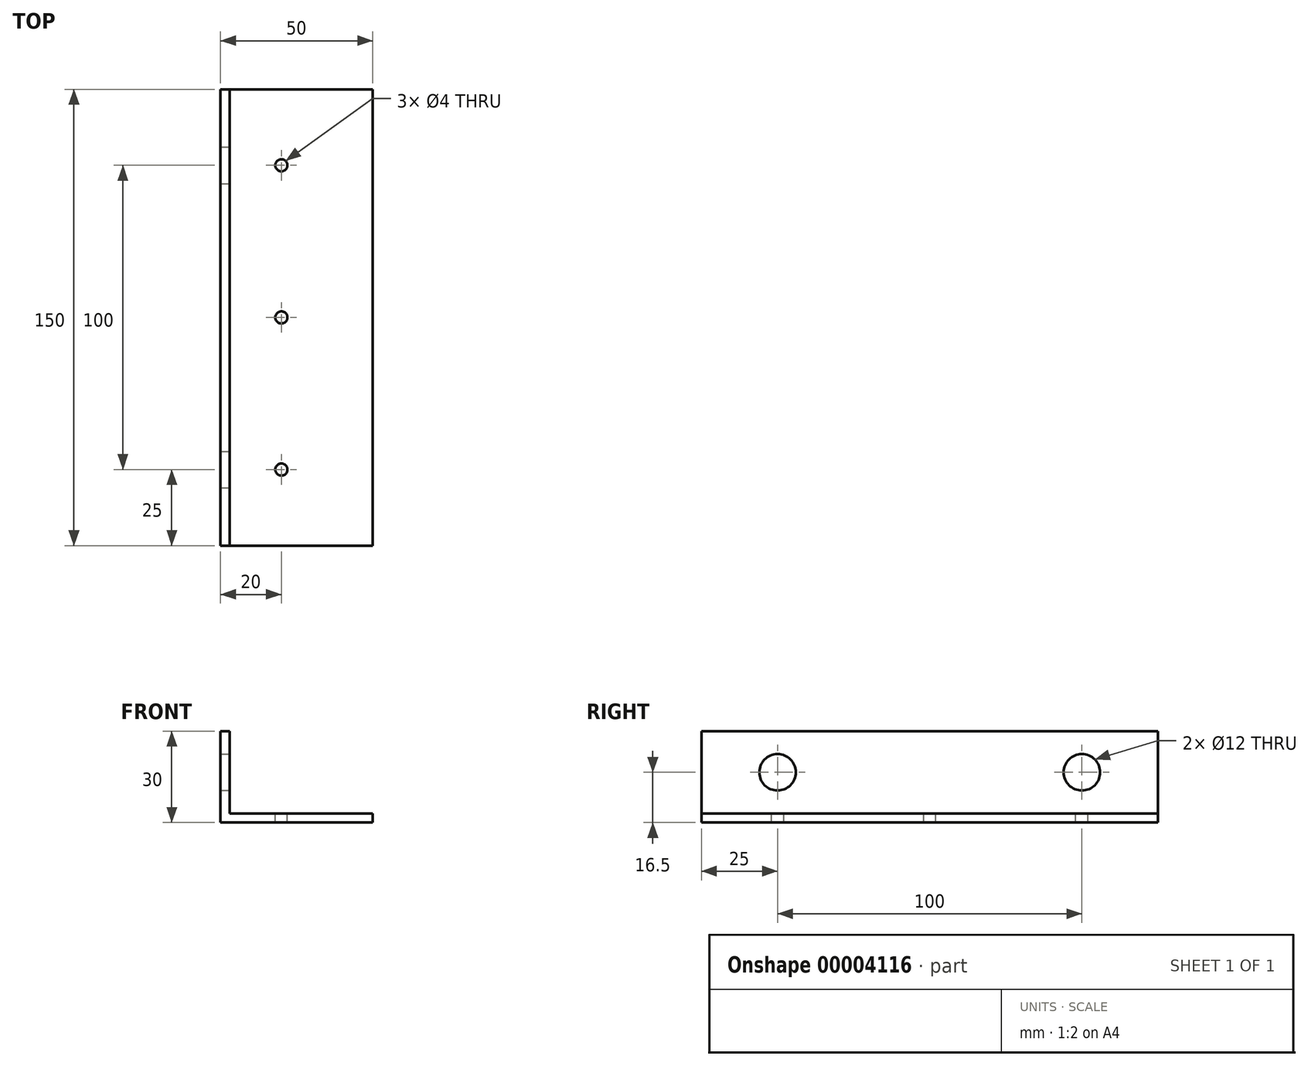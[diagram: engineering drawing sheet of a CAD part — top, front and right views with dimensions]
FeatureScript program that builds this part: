
annotation { "Feature Type Name" : "Feature", "Feature Type Description" : "" }
export const myFeature = defineFeature(function(context is Context, id is Id, definition is map)
    precondition{}
    {
        {
            var Q0;
            Q0=qCreatedBy(makeId("Front.planeOp"),FACE);
            var sketch = newSketch(context, id + "F0", { "sketchPlane" : qUnion([Q0])});
            skLineSegment(sketch, "E0", {"start": v(0, 0) * mm, "end": v(50, 0) * mm});
            skLineSegment(sketch, "E1", {"start": v(50, 3) * mm, "end": v(50, 0) * mm});
            skLineSegment(sketch, "E2", {"start": v(0, 0) * mm, "end": v(0, 30) * mm});
            skLineSegment(sketch, "E3", {"start": v(0, 30) * mm, "end": v(3, 30) * mm});
            skLineSegment(sketch, "E4", {"start": v(3, 30) * mm, "end": v(3, 3) * mm});
            skLineSegment(sketch, "E5", {"start": v(3, 3) * mm, "end": v(50, 3) * mm});
            skSolve(sketch);
        }
        {
            var Q0;
            Q0=makeQuery(id+"F0.imprint","IMPRINT",FACE,{"disambiguationData":[TD([[makeQuery(id+"F0.imprint","IMPRINT",EDGE,{"derivedFrom":sQuery(id+"F0.wireOp",EDGE,"E0")}),1.0]])]});
            extrude(context, id + "F1", {"entities" : qUnion([Q0]), "depth" : 150 * mm});
        }
        {
            var Q0;
            Q0=makeQuery(id+"F1.opExtrude","SWEPT_FACE",FACE,{"disambiguationData":[OSD([sQuery(id+"F0.wireOp",EDGE,"E4")])]});
            var sketch = newSketch(context, id + "F2", { "sketchPlane" : qUnion([Q0])});
            skLineSegment(sketch, "E6", {"start": v(-150, 16.5) * mm, "end": v(0, 16.5) * mm});
            skCircle(sketch, "E7", {"center": v(-125, 16.5) * mm, "radius": 6 * mm});
            skCircle(sketch, "E8", {"center": v(-25, 16.5) * mm, "radius": 6 * mm});
            skSolve(sketch);
        }
        {
            var Q0;
            {var subQ0=sQuery(id+"F2.wireOp",EDGE,"E7");var subQ1=sQuery(id+"F2.wireOp",EDGE,"E6");var subQ3=makeQuery(id+"F2.imprint","INTERSECT",VERTEX,{"disambiguationData":[OD(0.0)],"derivedFrom":[subQ1,subQ0]});Q0=makeQuery(id+"F2.imprint","IMPRINT",FACE,{"disambiguationData":[TD([[makeQuery(id+"F2.imprint","IMPRINT",EDGE,{"disambiguationData":[TD([[subQ3,-1.0]])],"derivedFrom":subQ1}),-1.0]])]});}
            var Q1;
            {var subQ0=sQuery(id+"F2.wireOp",EDGE,"E7");var subQ1=sQuery(id+"F2.wireOp",EDGE,"E6");var subQ3=makeQuery(id+"F2.imprint","INTERSECT",VERTEX,{"disambiguationData":[OD(0.0)],"derivedFrom":[subQ1,subQ0]});Q1=makeQuery(id+"F2.imprint","IMPRINT",FACE,{"disambiguationData":[TD([[makeQuery(id+"F2.imprint","IMPRINT",EDGE,{"disambiguationData":[TD([[subQ3,-1.0]])],"derivedFrom":subQ1}),1.0]])]});}
            var Q2;
            {var subQ0=sQuery(id+"F2.wireOp",EDGE,"E8");var subQ1=sQuery(id+"F2.wireOp",EDGE,"E6");var subQ3=makeQuery(id+"F2.imprint","INTERSECT",VERTEX,{"disambiguationData":[OD(0.0)],"derivedFrom":[subQ1,subQ0]});Q2=makeQuery(id+"F2.imprint","IMPRINT",FACE,{"disambiguationData":[TD([[makeQuery(id+"F2.imprint","IMPRINT",EDGE,{"disambiguationData":[TD([[subQ3,-1.0]])],"derivedFrom":subQ1}),1.0]])]});}
            var Q3;
            {var subQ0=sQuery(id+"F2.wireOp",EDGE,"E8");var subQ1=sQuery(id+"F2.wireOp",EDGE,"E6");var subQ3=makeQuery(id+"F2.imprint","INTERSECT",VERTEX,{"disambiguationData":[OD(0.0)],"derivedFrom":[subQ1,subQ0]});Q3=makeQuery(id+"F2.imprint","IMPRINT",FACE,{"disambiguationData":[TD([[makeQuery(id+"F2.imprint","IMPRINT",EDGE,{"disambiguationData":[TD([[subQ3,-1.0]])],"derivedFrom":subQ1}),-1.0]])]});}
            extrude(context, id + "F3", {"entities" : qUnion([Q0, Q1, Q2, Q3]), "operationType" : NewBodyOperationType.REMOVE, "oppositeDirection" : true, "depth" : 25 * mm});
        }
        {
            var Q0;
            Q0=makeQuery(id+"F1.opExtrude","SWEPT_FACE",FACE,{"disambiguationData":[OSD([sQuery(id+"F0.wireOp",EDGE,"E5")])]});
            var sketch = newSketch(context, id + "F4", { "sketchPlane" : qUnion([Q0])});
            skLineSegment(sketch, "E9", {"start": v(20, -150) * mm, "end": v(20, 0) * mm});
            skCircle(sketch, "E10", {"center": v(20, -125) * mm, "radius": 2 * mm});
            skCircle(sketch, "E11.0.1.0", {"center": v(20, -75) * mm, "radius": 2 * mm});
            skCircle(sketch, "E11.0.2.0", {"center": v(20, -25) * mm, "radius": 2 * mm});
            skLineSegment(sketch, "E11.direction1", {"start": v(20, -125) * mm, "end": v(45, -125) * mm, "construction": true});
            skLineSegment(sketch, "E11.direction2", {"start": v(20, -125) * mm, "end": v(20, -75) * mm, "construction": true});
            skSolve(sketch);
        }
        {
            var Q0;
            {var subQ0=sQuery(id+"F4.wireOp",EDGE,"E10");var subQ1=sQuery(id+"F4.wireOp",EDGE,"E9");var subQ3=makeQuery(id+"F4.imprint","INTERSECT",VERTEX,{"disambiguationData":[OD(0.0)],"derivedFrom":[subQ1,subQ0]});Q0=makeQuery(id+"F4.imprint","IMPRINT",FACE,{"disambiguationData":[TD([[makeQuery(id+"F4.imprint","IMPRINT",EDGE,{"disambiguationData":[TD([[subQ3,-1.0]])],"derivedFrom":subQ1}),-1.0]])]});}
            var Q1;
            {var subQ0=sQuery(id+"F4.wireOp",EDGE,"E10");var subQ1=sQuery(id+"F4.wireOp",EDGE,"E9");var subQ3=makeQuery(id+"F4.imprint","INTERSECT",VERTEX,{"disambiguationData":[OD(0.0)],"derivedFrom":[subQ1,subQ0]});Q1=makeQuery(id+"F4.imprint","IMPRINT",FACE,{"disambiguationData":[TD([[makeQuery(id+"F4.imprint","IMPRINT",EDGE,{"disambiguationData":[TD([[subQ3,-1.0]])],"derivedFrom":subQ1}),1.0]])]});}
            var Q2;
            {var subQ0=sQuery(id+"F4.wireOp",EDGE,"E11.0.1.0");var subQ1=sQuery(id+"F4.wireOp",EDGE,"E9");var subQ3=makeQuery(id+"F4.imprint","INTERSECT",VERTEX,{"disambiguationData":[OD(0.0)],"derivedFrom":[subQ1,subQ0]});Q2=makeQuery(id+"F4.imprint","IMPRINT",FACE,{"disambiguationData":[TD([[makeQuery(id+"F4.imprint","IMPRINT",EDGE,{"disambiguationData":[TD([[subQ3,-1.0]])],"derivedFrom":subQ1}),-1.0]])]});}
            var Q3;
            {var subQ0=sQuery(id+"F4.wireOp",EDGE,"E11.0.1.0");var subQ1=sQuery(id+"F4.wireOp",EDGE,"E9");var subQ3=makeQuery(id+"F4.imprint","INTERSECT",VERTEX,{"disambiguationData":[OD(0.0)],"derivedFrom":[subQ1,subQ0]});Q3=makeQuery(id+"F4.imprint","IMPRINT",FACE,{"disambiguationData":[TD([[makeQuery(id+"F4.imprint","IMPRINT",EDGE,{"disambiguationData":[TD([[subQ3,-1.0]])],"derivedFrom":subQ1}),1.0]])]});}
            var Q4;
            {var subQ0=sQuery(id+"F4.wireOp",EDGE,"E11.0.2.0");var subQ1=sQuery(id+"F4.wireOp",EDGE,"E9");var subQ3=makeQuery(id+"F4.imprint","INTERSECT",VERTEX,{"disambiguationData":[OD(0.0)],"derivedFrom":[subQ1,subQ0]});Q4=makeQuery(id+"F4.imprint","IMPRINT",FACE,{"disambiguationData":[TD([[makeQuery(id+"F4.imprint","IMPRINT",EDGE,{"disambiguationData":[TD([[subQ3,-1.0]])],"derivedFrom":subQ1}),-1.0]])]});}
            var Q5;
            {var subQ0=sQuery(id+"F4.wireOp",EDGE,"E11.0.2.0");var subQ1=sQuery(id+"F4.wireOp",EDGE,"E9");var subQ3=makeQuery(id+"F4.imprint","INTERSECT",VERTEX,{"disambiguationData":[OD(0.0)],"derivedFrom":[subQ1,subQ0]});Q5=makeQuery(id+"F4.imprint","IMPRINT",FACE,{"disambiguationData":[TD([[makeQuery(id+"F4.imprint","IMPRINT",EDGE,{"disambiguationData":[TD([[subQ3,-1.0]])],"derivedFrom":subQ1}),1.0]])]});}
            extrude(context, id + "F5", {"entities" : qUnion([Q0, Q1, Q2, Q3, Q4, Q5]), "operationType" : NewBodyOperationType.REMOVE, "oppositeDirection" : true, "depth" : 25 * mm});
        }
    });
